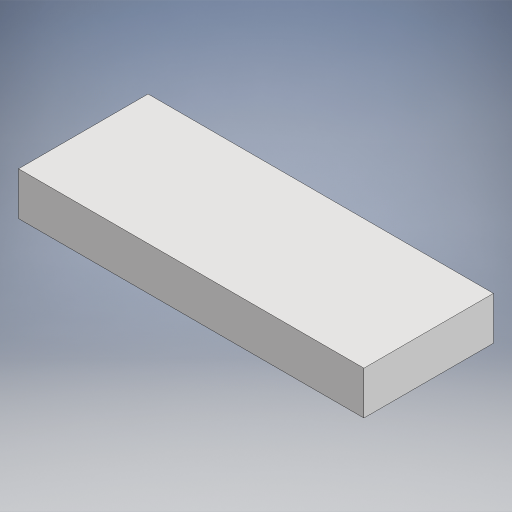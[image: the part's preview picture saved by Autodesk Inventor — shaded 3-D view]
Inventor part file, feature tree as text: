
AUTODESK INVENTOR PART (.ipt)
format: ipt  version: 2023.2 (Build 272271000, 271)  size: 214,016 bytes
history: native  units: in
note: dims shown in document units (in); Inventor stores cm internally (conversion verified against a paired STEP export)
features: extrude x1, sketch x1
ambient origin geometry x8: Origin, YZ Plane, XZ Plane, XY Plane, X Axis, Y Axis, Z Axis, Center Point
bodies: Solid1 (feature_tree)
feature tree (2):
  extrude  "Extrusion1"  Depth=18.0in
  sketch  "Sketch2"  dims[d3=6.0in d4=18.0in d5=48.0in d6=0.0in]
